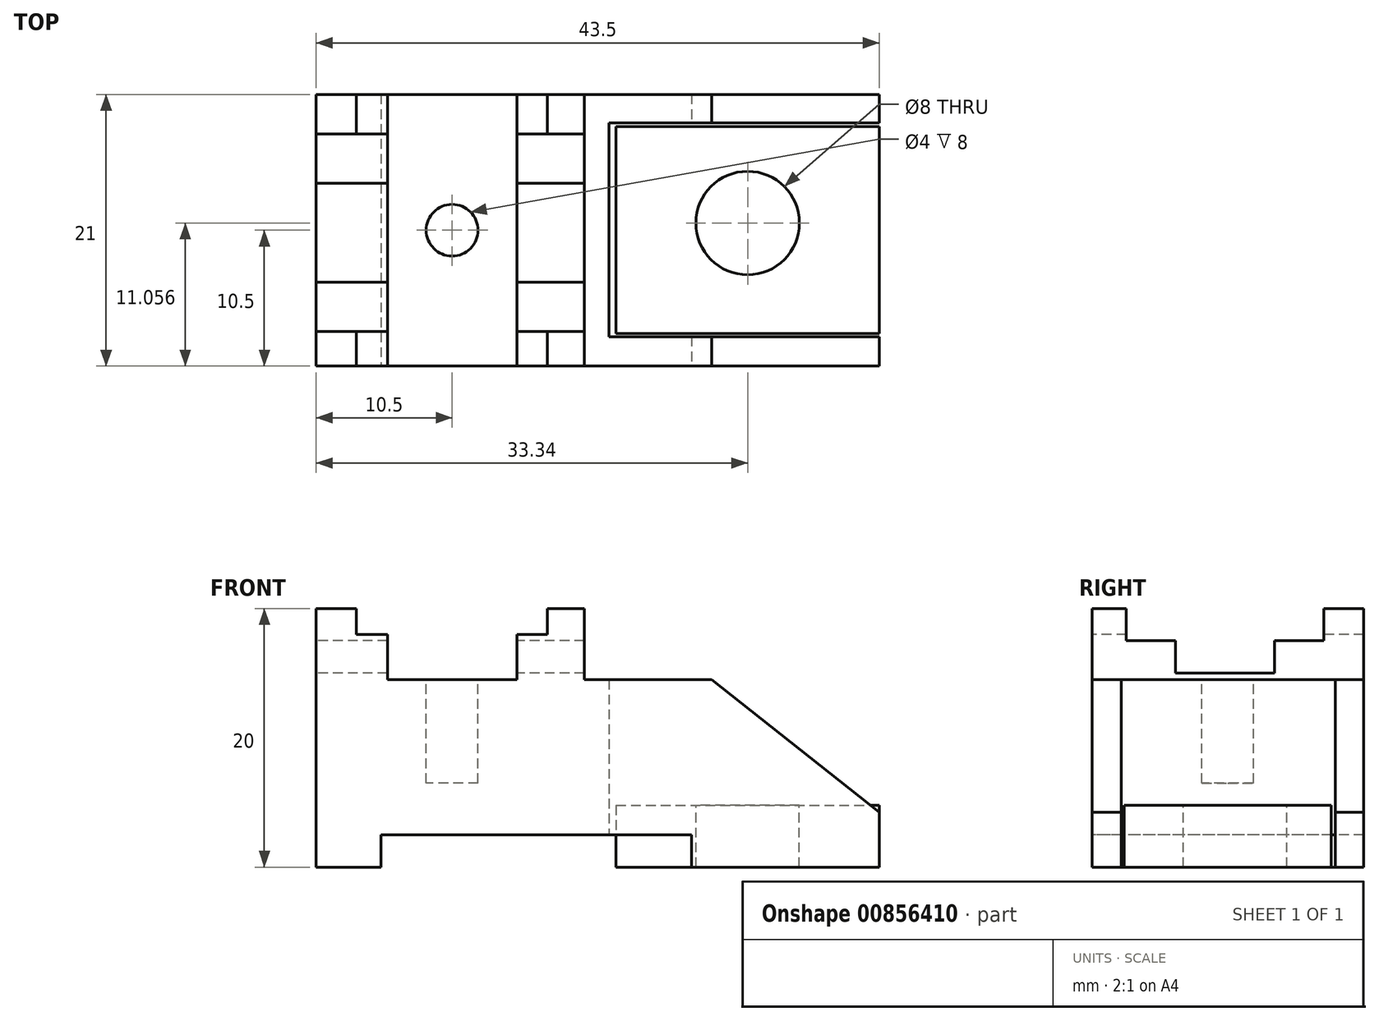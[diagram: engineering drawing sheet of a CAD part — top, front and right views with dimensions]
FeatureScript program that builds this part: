
annotation { "Feature Type Name" : "Feature", "Feature Type Description" : "" }
export const myFeature = defineFeature(function(context is Context, id is Id, definition is map)
    precondition{}
    {
        {
            var Q0;
            Q0=qCreatedBy(makeId("Front.planeOp"),FACE);
            var sketch = newSketch(context, id + "F0", { "sketchPlane" : qUnion([Q0])});
            skLineSegment(sketch, "E0.bottom", {"start": v(0, 0) * mm, "end": v(43.5, 0) * mm});
            skLineSegment(sketch, "E0.top", {"start": v(0, 20) * mm, "end": v(43.5, 20) * mm});
            skLineSegment(sketch, "E0.left", {"start": v(0, 0) * mm, "end": v(0, 20) * mm});
            skLineSegment(sketch, "E0.right", {"start": v(43.5, 0) * mm, "end": v(43.5, 20) * mm});
            skSolve(sketch);
        }
        {
            var Q0;
            Q0=makeQuery(id+"F0.imprint","IMPRINT",FACE,{"disambiguationData":[TD([[makeQuery(id+"F0.imprint","IMPRINT",EDGE,{"derivedFrom":sQuery(id+"F0.wireOp",EDGE,"E0.bottom")}),1.0]])]});
            extrude(context, id + "F1", {"entities" : qUnion([Q0]), "depth" : 21 * mm, "offsetDistance" : 25.4 * mm});
        }
        {
            var Q0;
            Q0=makeQuery(id+"F1.opExtrude","CAP_FACE",FACE,{"disambiguationData":[OSD([sQuery(id+"F0.wireOp",EDGE,"E0.bottom"),sQuery(id+"F0.wireOp",EDGE,"E0.top"),sQuery(id+"F0.wireOp",EDGE,"E0.left"),sQuery(id+"F0.wireOp",EDGE,"E0.right")])],"isStart":false});
            var sketch = newSketch(context, id + "F2", { "sketchPlane" : qUnion([Q0])});
            skLineSegment(sketch, "E1.bottom", {"start": v(5, 0) * mm, "end": v(29, 0) * mm});
            skLineSegment(sketch, "E1.top", {"start": v(5, 2.5) * mm, "end": v(29, 2.5) * mm});
            skLineSegment(sketch, "E1.left", {"start": v(5, 0) * mm, "end": v(5, 2.5) * mm});
            skLineSegment(sketch, "E1.right", {"start": v(29, 0) * mm, "end": v(29, 2.5) * mm});
            skLineSegment(sketch, "E2.bottom", {"start": v(5.5, 20) * mm, "end": v(15.5, 20) * mm});
            skLineSegment(sketch, "E2.top", {"start": v(5.5, 14.5) * mm, "end": v(15.5, 14.5) * mm});
            skLineSegment(sketch, "E2.left", {"start": v(5.5, 20) * mm, "end": v(5.5, 14.5) * mm});
            skLineSegment(sketch, "E2.right", {"start": v(15.5, 20) * mm, "end": v(15.5, 14.5) * mm});
            skLineSegment(sketch, "E3.bottom", {"start": v(3.1, 20) * mm, "end": v(5.5, 20) * mm});
            skLineSegment(sketch, "E3.top", {"start": v(3.1, 18) * mm, "end": v(5.5, 18) * mm});
            skLineSegment(sketch, "E3.left", {"start": v(3.1, 20) * mm, "end": v(3.1, 18) * mm});
            skLineSegment(sketch, "E3.right", {"start": v(5.5, 20) * mm, "end": v(5.5, 18) * mm});
            skLineSegment(sketch, "E4.bottom", {"start": v(15.5, 18) * mm, "end": v(17.85, 18) * mm});
            skLineSegment(sketch, "E4.top", {"start": v(15.5, 20) * mm, "end": v(17.85, 20) * mm});
            skLineSegment(sketch, "E4.left", {"start": v(15.5, 18) * mm, "end": v(15.5, 20) * mm});
            skLineSegment(sketch, "E4.right", {"start": v(17.85, 18) * mm, "end": v(17.85, 20) * mm});
            skSolve(sketch);
        }
        {
            var Q0;
            Q0=makeQuery(id+"F2.imprint","IMPRINT",FACE,{"disambiguationData":[TD([[makeQuery(id+"F2.imprint","IMPRINT",EDGE,{"derivedFrom":sQuery(id+"F2.wireOp",EDGE,"E2.bottom")}),-1.0]])]});
            var Q1;
            Q1=makeQuery(id+"F2.imprint","IMPRINT",FACE,{"disambiguationData":[TD([[makeQuery(id+"F2.imprint","IMPRINT",EDGE,{"derivedFrom":sQuery(id+"F2.wireOp",EDGE,"E1.bottom")}),1.0]])]});
            var Q2;
            Q2=makeQuery(id+"F2.imprint","IMPRINT",FACE,{"disambiguationData":[TD([[makeQuery(id+"F2.imprint","IMPRINT",EDGE,{"derivedFrom":sQuery(id+"F2.wireOp",EDGE,"E3.bottom")}),-1.0]])]});
            var Q3;
            Q3=makeQuery(id+"F2.imprint","IMPRINT",FACE,{"disambiguationData":[TD([[makeQuery(id+"F2.imprint","IMPRINT",EDGE,{"derivedFrom":sQuery(id+"F2.wireOp",EDGE,"E4.bottom")}),1.0]])]});
            extrude(context, id + "F3", {"entities" : qUnion([Q0, Q1, Q2, Q3]), "operationType" : NewBodyOperationType.REMOVE, "endBound" : BoundingType.THROUGH_ALL, "oppositeDirection" : true, "depth" : 25.4 * mm, "offsetDistance" : 25.4 * mm});
        }
        {
            var Q0;
            Q0=makeQuery(id+"F1.opExtrude","CAP_FACE",FACE,{"disambiguationData":[OSD([sQuery(id+"F0.wireOp",EDGE,"E0.bottom"),sQuery(id+"F0.wireOp",EDGE,"E0.top"),sQuery(id+"F0.wireOp",EDGE,"E0.left"),sQuery(id+"F0.wireOp",EDGE,"E0.right")])],"isStart":false});
            var sketch = newSketch(context, id + "F4", { "sketchPlane" : qUnion([Q0])});
            skLineSegment(sketch, "E5", {"start": v(23.58, 20) * mm, "end": v(43.5, 4.25) * mm});
            skSolve(sketch);
        }
        {
            var Q0;
            Q0 = qSketchRegion(id + "F4", true);
            var Q1;
            {var subQ0=sQuery(id+"F4.wireOp",EDGE,"E5");Q1=makeQuery(id+"F4.imprint","IMPRINT",FACE,{"disambiguationData":[TD([[makeQuery(id+"F4.imprint","IMPRINT",EDGE,{"derivedFrom":subQ0}),1.0]])]});}
            extrude(context, id + "F5", {"entities" : qUnion([Q0, Q1]), "operationType" : NewBodyOperationType.REMOVE, "endBound" : BoundingType.THROUGH_ALL, "oppositeDirection" : true, "depth" : 25.4 * mm, "offsetDistance" : 25.4 * mm});
        }
        {
            var Q0;
            Q0=makeQuery(id+"F3.boolean.opBoolean","COPY",FACE,{"derivedFrom":makeQuery(id+"F3.opExtrude","SWEPT_FACE",FACE,{"disambiguationData":[OSD([sQuery(id+"F2.wireOp",EDGE,"E2.top")])]})});
            var sketch = newSketch(context, id + "F6", { "sketchPlane" : qUnion([Q0])});
            skLineSegment(sketch, "E6", {"start": v(10.5, 0) * mm, "end": v(10.5, -21) * mm, "construction": true});
            skPoint(sketch, "E7.endSnap0", {"position": v(15.5, -10.5) * mm});
            skCircle(sketch, "E8", {"center": v(10.5, -10.5) * mm, "radius": 2 * mm});
            skSolve(sketch);
        }
        {
            var Q0;
            Q0=makeQuery(id+"F6.imprint","IMPRINT",FACE,{"disambiguationData":[TD([[makeQuery(id+"F6.imprint","IMPRINT",EDGE,{"derivedFrom":sQuery(id+"F6.wireOp",EDGE,"E8")}),1.0]])]});
            extrude(context, id + "F7", {"entities" : qUnion([Q0]), "operationType" : NewBodyOperationType.REMOVE, "oppositeDirection" : true, "depth" : 8 * mm, "offsetDistance" : 25.4 * mm});
        }
        {
            var Q0;
            {var subQ0=sQuery(id+"F0.wireOp",EDGE,"E0.right");var subQ3=sQuery(id+"F0.wireOp",EDGE,"E0.bottom");Q0=makeQuery(id+"F3.boolean.opBoolean","SPLIT",FACE,{"disambiguationData":[TD([makeQuery(id+"F1.opExtrude","SWEPT_FACE",FACE,{"disambiguationData":[OSD([subQ0])]})])],"derivedFrom":makeQuery(id+"F1.opExtrude","SWEPT_FACE",FACE,{"disambiguationData":[OSD([subQ3])]})});}
            var sketch = newSketch(context, id + "F8", { "sketchPlane" : qUnion([Q0])});
            skLineSegment(sketch, "E9", {"start": v(36.25, 21) * mm, "end": v(36.25, 0) * mm, "construction": true});
            skLineSegment(sketch, "E10", {"start": v(43.5, 10.5) * mm, "end": v(29, 10.5) * mm, "construction": true});
            skCircle(sketch, "E11", {"center": v(36.25, 10.5) * mm, "radius": 4 * mm});
            skSolve(sketch);
        }
        {
            var Q0;
            Q0=makeQuery(id+"F1.opExtrude","SWEPT_FACE",FACE,{"disambiguationData":[OSD([sQuery(id+"F0.wireOp",EDGE,"E0.left")])]});
            var sketch = newSketch(context, id + "F9", { "sketchPlane" : qUnion([Q0])});
            skLineSegment(sketch, "E12.bottom", {"start": v(3.07, 20) * mm, "end": v(18.34, 20) * mm});
            skLineSegment(sketch, "E12.top", {"start": v(3.07, 17.5) * mm, "end": v(18.34, 17.5) * mm});
            skLineSegment(sketch, "E12.left", {"start": v(3.07, 20) * mm, "end": v(3.07, 17.5) * mm});
            skLineSegment(sketch, "E12.right", {"start": v(18.34, 20) * mm, "end": v(18.34, 17.5) * mm});
            skSolve(sketch);
        }
        {
            var Q0;
            Q0=makeQuery(id+"F9.imprint","IMPRINT",FACE,{"disambiguationData":[TD([[makeQuery(id+"F9.imprint","IMPRINT",EDGE,{"derivedFrom":sQuery(id+"F9.wireOp",EDGE,"E12.bottom")}),1.0]])]});
            extrude(context, id + "F10", {"entities" : qUnion([Q0]), "operationType" : NewBodyOperationType.REMOVE, "endBound" : BoundingType.THROUGH_ALL, "oppositeDirection" : true, "depth" : 25.4 * mm, "offsetDistance" : 25.4 * mm});
        }
        {
            var Q0;
            Q0=makeQuery(id+"F1.opExtrude","SWEPT_FACE",FACE,{"disambiguationData":[OSD([sQuery(id+"F0.wireOp",EDGE,"E0.left")])]});
            var sketch = newSketch(context, id + "F11", { "sketchPlane" : qUnion([Q0])});
            skLineSegment(sketch, "E13.bottom", {"start": v(6.88, 17.5) * mm, "end": v(14.53, 17.5) * mm});
            skLineSegment(sketch, "E13.top", {"start": v(6.88, 15) * mm, "end": v(14.53, 15) * mm});
            skLineSegment(sketch, "E13.left", {"start": v(6.88, 17.5) * mm, "end": v(6.88, 15) * mm});
            skLineSegment(sketch, "E13.right", {"start": v(14.53, 17.5) * mm, "end": v(14.53, 15) * mm});
            skSolve(sketch);
        }
        {
            var Q0;
            Q0=makeQuery(id+"F11.imprint","IMPRINT",FACE,{"disambiguationData":[TD([[makeQuery(id+"F11.imprint","IMPRINT",EDGE,{"derivedFrom":sQuery(id+"F11.wireOp",EDGE,"E13.bottom")}),-1.0]])]});
            extrude(context, id + "F12", {"entities" : qUnion([Q0]), "operationType" : NewBodyOperationType.REMOVE, "endBound" : BoundingType.THROUGH_ALL, "oppositeDirection" : true, "depth" : 25.4 * mm, "offsetDistance" : 25.4 * mm});
        }
        {
            var Q0;
            Q0=qCreatedBy(makeId("Top.planeOp"),FACE);
            var sketch = newSketch(context, id + "F13", { "sketchPlane" : qUnion([Q0])});
            skLineSegment(sketch, "E14.bottom", {"start": v(23.18, -2.5) * mm, "end": v(43.5, -2.5) * mm});
            skLineSegment(sketch, "E14.top", {"start": v(23.18, -18.5) * mm, "end": v(43.5, -18.5) * mm});
            skLineSegment(sketch, "E14.left", {"start": v(23.18, -2.5) * mm, "end": v(23.18, -18.5) * mm});
            skLineSegment(sketch, "E14.right", {"start": v(43.5, -2.5) * mm, "end": v(43.5, -18.5) * mm});
            skSolve(sketch);
        }
        {
            var Q0;
            Q0=makeQuery(id+"F1.opExtrude","CAP_FACE",FACE,{"disambiguationData":[OSD([sQuery(id+"F0.wireOp",EDGE,"E0.bottom"),sQuery(id+"F0.wireOp",EDGE,"E0.top"),sQuery(id+"F0.wireOp",EDGE,"E0.left"),sQuery(id+"F0.wireOp",EDGE,"E0.right")])],"isStart":false});
            var sketch = newSketch(context, id + "F14", { "sketchPlane" : qUnion([Q0])});
            skLineSegment(sketch, "E15.bottom", {"start": v(20.71, 20) * mm, "end": v(30.56, 20) * mm});
            skLineSegment(sketch, "E15.top", {"start": v(20.71, 14.49) * mm, "end": v(30.56, 14.49) * mm});
            skLineSegment(sketch, "E15.left", {"start": v(20.71, 20) * mm, "end": v(20.71, 14.49) * mm});
            skLineSegment(sketch, "E15.right", {"start": v(30.56, 20) * mm, "end": v(30.56, 14.49) * mm});
            skLineSegment(sketch, "E16", {"start": v(0, 14.47) * mm, "end": v(35.26, 14.47) * mm, "construction": true});
            skSolve(sketch);
        }
        {
            var Q0;
            {var subQ3=sQuery(id+"F14.wireOp",EDGE,"E15.left");Q0=makeQuery(id+"F14.imprint","IMPRINT",FACE,{"disambiguationData":[TD([[makeQuery(id+"F14.imprint","IMPRINT",EDGE,{"derivedFrom":subQ3}),1.0]])]});}
            extrude(context, id + "F15", {"entities" : qUnion([Q0]), "operationType" : NewBodyOperationType.REMOVE, "endBound" : BoundingType.THROUGH_ALL, "oppositeDirection" : true, "depth" : 25.4 * mm, "offsetDistance" : 25.4 * mm});
        }
        {
            var Q0;
            Q0=qCreatedBy(makeId("Top.planeOp"),FACE);
            var sketch = newSketch(context, id + "F16", { "sketchPlane" : qUnion([Q0])});
            skLineSegment(sketch, "E17.bottom", {"start": v(46.37, -2.2) * mm, "end": v(22.62, -2.2) * mm});
            skLineSegment(sketch, "E17.top", {"start": v(46.37, -18.74) * mm, "end": v(22.62, -18.74) * mm});
            skLineSegment(sketch, "E17.left", {"start": v(46.37, -2.2) * mm, "end": v(46.37, -18.74) * mm});
            skLineSegment(sketch, "E17.right", {"start": v(22.62, -2.2) * mm, "end": v(22.62, -18.74) * mm});
            skSolve(sketch);
        }
        {
            var Q0;
            Q0 = qSketchRegion(id + "F16", true);
            extrude(context, id + "F17", {"entities" : qUnion([Q0]), "operationType" : NewBodyOperationType.REMOVE, "depth" : 25.4 * mm, "offsetDistance" : 25.4 * mm});
        }
        {
            var Q0;
            Q0=makeQuery(id+"F13.imprint","IMPRINT",FACE,{"disambiguationData":[TD([[makeQuery(id+"F13.imprint","IMPRINT",EDGE,{"derivedFrom":sQuery(id+"F13.wireOp",EDGE,"E14.bottom")}),-1.0]])]});
            extrude(context, id + "F18", {"entities" : qUnion([Q0]), "depth" : 4.78 * mm, "offsetDistance" : 25.4 * mm});
        }
        {
            var Q0;
            Q0=makeQuery(id+"F8.imprint","IMPRINT",FACE,{"disambiguationData":[TD([[makeQuery(id+"F8.imprint","IMPRINT",EDGE,{"derivedFrom":sQuery(id+"F8.wireOp",EDGE,"E11")}),1.0]])]});
            extrude(context, id + "F19", {"entities" : qUnion([Q0]), "operationType" : NewBodyOperationType.REMOVE, "endBound" : BoundingType.THROUGH_ALL, "depth" : 25.4 * mm, "offsetDistance" : 25.4 * mm});
        }
        {
            var Q0;
            Q0=makeQuery(id+"F18.opExtrude","CAP_FACE",FACE,{"disambiguationData":[OSD([sQuery(id+"F13.wireOp",EDGE,"E14.bottom"),sQuery(id+"F13.wireOp",EDGE,"E14.top"),sQuery(id+"F13.wireOp",EDGE,"E14.left"),sQuery(id+"F13.wireOp",EDGE,"E14.right")])],"isStart":false});
            var sketch = newSketch(context, id + "F20", { "sketchPlane" : qUnion([Q0])});
            skCircle(sketch, "E18", {"center": v(33.34, -9.94) * mm, "radius": 4 * mm});
            skPoint(sketch, "E18.centerSnap0", {"position": v(33.34, -2.5) * mm});
            skSolve(sketch);
        }
        {
            var Q0;
            Q0=makeQuery(id+"F20.imprint","IMPRINT",FACE,{"disambiguationData":[TD([[makeQuery(id+"F20.imprint","IMPRINT",EDGE,{"derivedFrom":sQuery(id+"F20.wireOp",EDGE,"E18")}),1.0]])]});
            extrude(context, id + "F21", {"entities" : qUnion([Q0]), "operationType" : NewBodyOperationType.REMOVE, "endBound" : BoundingType.THROUGH_ALL, "oppositeDirection" : true, "depth" : 25.4 * mm, "offsetDistance" : 25.4 * mm});
        }
    });
